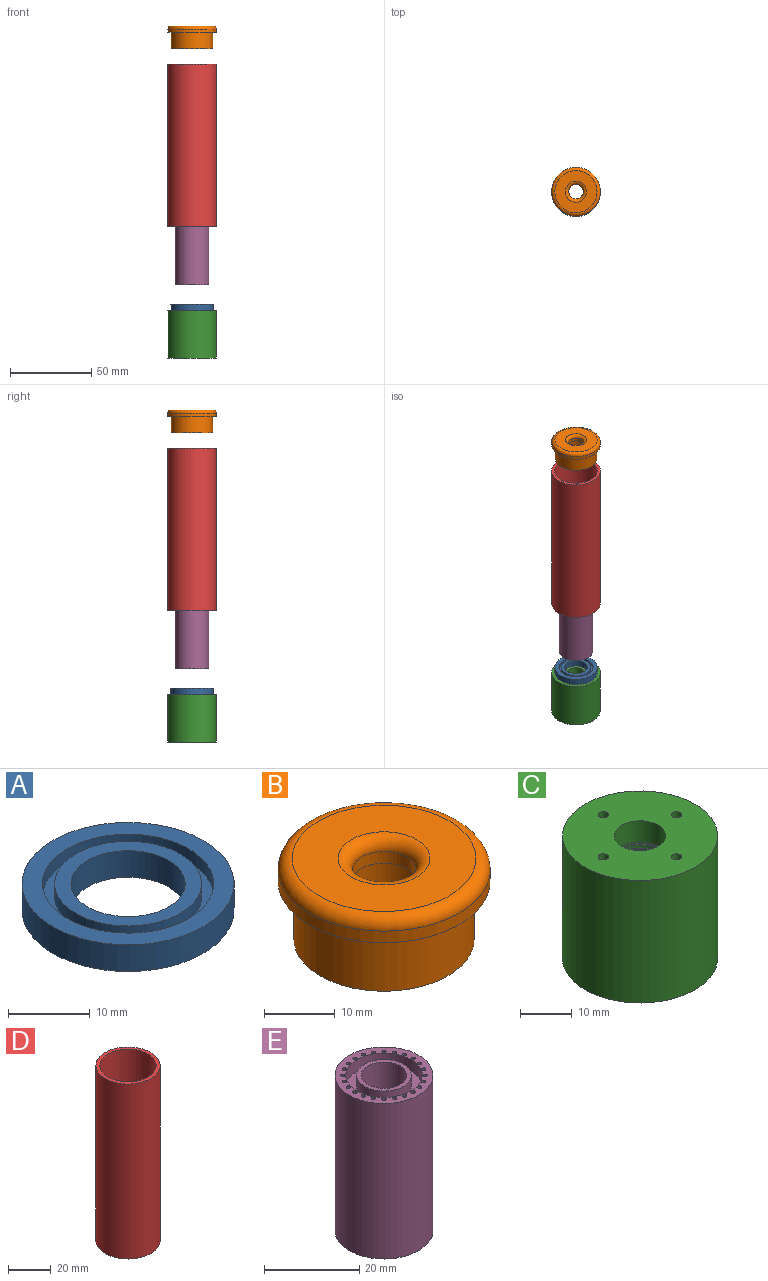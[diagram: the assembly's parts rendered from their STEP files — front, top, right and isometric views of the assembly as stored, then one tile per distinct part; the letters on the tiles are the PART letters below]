
ASSEMBLY  parts=5 mates=4
PART A: 20 faces, bbox 26x26x6 mm
  f0: plane 18x18mm, normal (0,0,1), area 100.5mm2, adj f1,f17
  f1: cylinder r=7mm len=14mm, axis (0,0,-1), area 175.9mm2, adj f0,f4
  f2: cylinder r=13mm len=26mm, axis (0,0,-1), area 326.7mm2, adj f3,f4
  f3: plane 26x26mm, normal (0,0,1), area 184.6mm2, adj f2,f18
  f4: plane 26x26mm, normal (0,0,-1), area 369.9mm2, adj f1,f2,f5,f7,f9,f11
  f5: cylinder r=0.75mm len=1.5mm, axis (0,0,1), area 7.1mm2, adj f4,f16
  f6: plane 0.5x0.5mm, normal (0,0,-1), area 0.2mm2, adj f16
  f7: cylinder r=0.75mm len=1.5mm, axis (0,0,1), area 7.1mm2, adj f4,f13
  f8: plane 0.5x0.5mm, normal (0,0,-1), area 0.2mm2, adj f13
  f9: cylinder r=0.75mm len=1.5mm, axis (0,0,1), area 7.1mm2, adj f4,f14
  f10: plane 0.5x0.5mm, normal (0,0,-1), area 0.2mm2, adj f14
  f11: cylinder r=0.75mm len=1.5mm, axis (0,0,1), area 7.1mm2, adj f4,f15
  f12: plane 0.5x0.5mm, normal (0,0,-1), area 0.2mm2, adj f15
  f13: torus R=0.25mm, axis (0,0,1), area 2.8mm2, adj f7,f8
  f14: torus R=0.25mm, axis (0,0,1), area 2.8mm2, adj f9,f10
  f15: torus R=0.25mm, axis (0,0,1), area 2.8mm2, adj f11,f12
  f16: torus R=0.25mm, axis (0,0,1), area 2.8mm2, adj f5,f6
  f17: cylinder r=9mm len=18mm, axis (0,0,1), area 113.1mm2, adj f0,f19
  f18: cylinder r=10.5mm len=21mm, axis (0,0,1), area 131.9mm2, adj f3,f19
  f19: plane 21x21mm, normal (0,0,1), area 91.9mm2, adj f17,f18
PART B: 10 faces, bbox 32.5x32.5x14 mm
  f0: plane 12x12mm, normal (0,0,-1), area 49.5mm2, adj f1,f5
  f1: cylinder r=4.5mm len=9mm, axis (0,0,-1), area 56.5mm2, adj f0,f8
  f2: cylinder r=15mm len=30mm, axis (0,0,-1), area 188.5mm2, adj f4,f9
  f3: plane 26x26mm, normal (0,0,1), area 398.2mm2, adj f8,f9
  f4: plane 30x30mm, normal (0,0,-1), area 196.2mm2, adj f2,f6
  f5: cylinder r=6mm len=12mm, axis (0,0,1), area 377mm2, adj f0,f7
  f6: cylinder r=12.75mm len=25.5mm, axis (0,0,1), area 801.1mm2, adj f4,f7
  f7: plane 25.5x25.5mm, normal (0,0,-1), area 397.6mm2, adj f5,f6
  f8: torus R=6.5mm, axis (0,0,1), area 103.2mm2, adj f1,f3
  f9: torus R=13mm, axis (0,0,1), area 281.7mm2, adj f2,f3
PART C: 20 faces, bbox 30.1x30.1x29.1 mm
  f0: plane 19.58x19.58mm, normal (0,0,-1), area 140.7mm2, adj f1,f4,f5,f18
  f1: plane 0.2x0.1mm, normal (0,1,0), area 0mm2, adj f0,f3,f5
  f2: plane 0.2x0.1mm, normal (0,-1,0), area 0mm2, adj f4,f5,f9
  f3: bspline ~16.4x14.2mm, area 118.1mm2, adj f1,f4,f5,f9
  f4: bspline ~16.4x14.2mm, area 118.1mm2, adj f0,f2,f3,f5
  f5: cylinder r=7.1mm len=14.2mm, axis (0,0,-1), area 336.1mm2, adj f0,f1,f2,f3,f4,f9
  f6: cylinder r=15mm len=30mm, axis (0,0,-1), area 2733.2mm2, adj f8,f19
  f7: cylinder r=5mm len=10mm, axis (0,0,-1), area 157.1mm2, adj f8,f9
  f8: plane 30x30mm, normal (0,0,1), area 615.8mm2, adj f6,f7,f10,f12,f14,f16
  f9: plane 14.28x14.28mm, normal (0,0,-1), area 79.4mm2, adj f2,f3,f5,f7
  f10: cylinder r=1mm len=2.5mm, axis (0,0,1), area 15.7mm2, adj f8,f11
  f11: plane 2x2mm, normal (0,0,1), area 3.1mm2, adj f10
  f12: cylinder r=1mm len=2.5mm, axis (0,0,1), area 15.7mm2, adj f8,f13
  f13: plane 2x2mm, normal (0,0,1), area 3.1mm2, adj f12
  f14: cylinder r=1mm len=2.5mm, axis (0,0,1), area 15.7mm2, adj f8,f15
  f15: plane 2x2mm, normal (0,0,1), area 3.1mm2, adj f14
  f16: cylinder r=1mm len=2.5mm, axis (0,0,1), area 15.7mm2, adj f8,f17
  f17: plane 2x2mm, normal (0,0,1), area 3.1mm2, adj f16
  f18: cylinder r=9.75mm len=19.5mm, axis (0,0,1), area 735.1mm2, adj f0,f19
  f19: plane 30x30mm, normal (0,0,-1), area 408.2mm2, adj f6,f18
PART D: 4 faces, bbox 30x30x100 mm
  f0: cylinder r=13.15mm len=100mm, axis (0,0,-1), area 8262.4mm2, adj f2,f3
  f1: cylinder r=15mm len=100mm, axis (0,0,-1), area 9424.8mm2, adj f2,f3
  f2: plane 30x30mm, normal (0,0,1), area 163.6mm2, adj f0,f1
  f3: plane 30x30mm, normal (0,0,-1), area 163.6mm2, adj f0,f1
PART E: 34 faces, bbox 20.6x20.6x40 mm
  f0: plane 11.5x11.5mm, normal (0,0,1), area 31.5mm2, adj f4,f7
  f1: plane 20.6x20.6mm, normal (0,0,-1), area 61.6mm2, adj f2,f6
  f2: cylinder r=10.3mm len=40mm, axis (0,0,1), area 2588.7mm2, adj f1,f3
  f3: plane 20.6x20.6mm, normal (0,0,1), area 114.4mm2, adj f2,f8,f10,f11,f12,f13,f14,f15
  f4: cylinder r=4.8mm len=20.77mm, axis (0,0,1), area 626.5mm2, adj f0,f5
  f5: cone r=9.3mm half-angle=15.9deg, axis (0,0,1), area 670.3mm2, adj f4,f6,f10,f11,f12,f13,f14,f15
  f6: cylinder r=9.3mm len=35mm, axis (0,0,1), area 2045.2mm2, adj f1,f5
  f7: cylinder r=5.75mm len=11.5mm, axis (0,0,1), area 108.4mm2, adj f0,f9
  f8: cylinder r=8.05mm len=16.1mm, axis (0,0,1), area 151.7mm2, adj f3,f9
  f9: plane 16.1x16.1mm, normal (0,0,1), area 99.7mm2, adj f7,f8
  f10: cylinder r=0.45mm len=8.9mm, axis (0,0,1), area 20.6mm2, adj f3,f5
  f11: cylinder r=0.45mm len=8.9mm, axis (0,0,1), area 20.6mm2, adj f3,f5
  f12: cylinder r=0.45mm len=8.9mm, axis (0,0,1), area 20.6mm2, adj f3,f5
  f13: cylinder r=0.45mm len=8.9mm, axis (0,0,1), area 20.6mm2, adj f3,f5
  f14: cylinder r=0.45mm len=8.9mm, axis (0,0,1), area 20.6mm2, adj f3,f5
  f15: cylinder r=0.45mm len=8.9mm, axis (0,0,1), area 20.6mm2, adj f3,f5
  f16: cylinder r=0.45mm len=8.9mm, axis (0,0,1), area 20.6mm2, adj f3,f5
  f17: cylinder r=0.45mm len=8.9mm, axis (0,0,1), area 20.6mm2, adj f3,f5
  f18: cylinder r=0.45mm len=8.9mm, axis (0,0,1), area 20.6mm2, adj f3,f5
  f19: cylinder r=0.45mm len=8.9mm, axis (0,0,1), area 20.6mm2, adj f3,f5
  f20: cylinder r=0.45mm len=8.9mm, axis (0,0,1), area 20.6mm2, adj f3,f5
  f21: cylinder r=0.45mm len=8.9mm, axis (0,0,1), area 20.6mm2, adj f3,f5
  f22: cylinder r=0.45mm len=8.9mm, axis (0,0,1), area 20.6mm2, adj f3,f5
  f23: cylinder r=0.45mm len=8.9mm, axis (0,0,1), area 20.6mm2, adj f3,f5
  f24: cylinder r=0.45mm len=8.9mm, axis (0,0,1), area 20.6mm2, adj f3,f5
  f25: cylinder r=0.45mm len=8.9mm, axis (0,0,1), area 20.6mm2, adj f3,f5
  f26: cylinder r=0.45mm len=8.9mm, axis (0,0,1), area 20.6mm2, adj f3,f5
  f27: cylinder r=0.45mm len=8.9mm, axis (0,0,1), area 20.6mm2, adj f3,f5
  f28: cylinder r=0.45mm len=8.9mm, axis (0,0,1), area 20.6mm2, adj f3,f5
  f29: cylinder r=0.45mm len=8.9mm, axis (0,0,1), area 20.6mm2, adj f3,f5
  f30: cylinder r=0.45mm len=8.9mm, axis (0,0,1), area 20.6mm2, adj f3,f5
  f31: cylinder r=0.45mm len=8.9mm, axis (0,0,1), area 20.6mm2, adj f3,f5
  f32: cylinder r=0.45mm len=8.9mm, axis (0,0,1), area 20.6mm2, adj f3,f5
  f33: cylinder r=0.45mm len=8.9mm, axis (0,0,1), area 20.6mm2, adj f3,f5
PLACE A t=(88.39,160.91,-7.63)mm
PLACE B t=(88.39,160.91,163.9)mm
PLACE C t=(88.39,160.91,-24.63)mm
PLACE D t=(88.39,160.91,44.49)mm
PLACE E rot(axis=(0,0,1),0deg) t=(88.39,160.91,8.52)mm
MATE cylindrical D.f0 <-> B.f5  axis (0,0,-1) through (88.39,160.91,144.49)mm
MATE cylindrical A.f2 <-> D.f0  axis (0,0,-1) through (88.39,160.91,-5.63)mm
MATE fastened C.f12 <-> A.f5  axis (0,0,1) through (88.39,150.91,-7.63)mm
MATE cylindrical A.f17 <-> E.f2  axis (0,0,1) through (88.39,160.91,-3.63)mm
